# Revit family: 0068079
name_source: partatom
category: Lighting Fixtures
revit_build: Autodesk Revit 2017 (Build: 20190507_1515(x64)
units: mm (PartAtom-declared; Revit-internal decimal feet)

## family parameters
Cut with Voids When Loaded = No
Host = Face
Light Source = Yes
OmniClass Number = 23.80.70.11.14
OmniClass Title = General Luminaries, Directional
Part Type = Normal
Room Calculation Point = No
Round Connector Dimension = Use Diameter
Shared = No

## types (2) — shared parameters
AccessoryMaterial = Diffuser-Sylvania-Glow
Apparent Load = 24 VA
Assembly Code = D5020200
AssetType = Fixed
BodyMaterial = Body-Sylvania-Gray
ClassificationName = Uniclass2015
ClassificationValue = EF_70_80
Color Filter = 16777215
Default Elevation = 1219 mm
Description = Start Waterproof, integrated LED weatherproof luminaire, with UV stabilized flat diffuser and linear prisms designed to achieve uniform lit appearance, optimise light output and to reduce glare, stainless steel diffuser clips and fixing brackets for surface mounting. Glass Reinforced Plastic housing for robustness, Polycarbonate diffuser, 2750 lm, 24 W, 115 lm/W, 4000 K, drive current 350 mA, Non dimmable, 3 hours emergency,  CRI80, IP65, IK08, Class I,  nominal average life (h):50000, 1278 mm x 84 mm x 75 mm ,energy class: A++ A+ A, D-mark
DiffuserMaterial = Diffuser-Sylvania-Transparent
Dimming Lamp Color Temperature Shift = <None>
DocumentationLiterature = http://www.sylvania-lighting.com
DurationUnit = hours
ElectricShockClassification = Class I
Emit Shape Visible in Rendering = No
Emit from Rectangle Length = 1252 mm  [stored 4.10761 ft]
Emit from Rectangle Width = 64 mm  [stored 0.209974 ft]
ExpectedLife = 50000
IfcExportAs = IfcLightFixtureType
IfcExportType = IfcLightFixtureType
ImpactProtectionIndex = IK08
IngressProtection = IP65
Keynote = 16500
Lamp = LED
LampColourRenderingIndex = 80
LampColourTemperature = 4000 K
LampsType = LED
Length = 1272 mm  [stored 4.17323 ft]
Manufacturer = Feilo Sylvania
ManufacturerName = Feilo Sylvania
Material = composite material housing, pc polycarbonate diffuser
ModelNumber = 0068079
NominalHeight = 75 mm
NominalLength = 1278 mm  [stored 4.19291 ft]
PowerConsumption = 24 W
PowerFactor = 0.95
ReflectorMaterial = <By Category>
Tilt Angle = -90.00°
Type Image = <None>
URL = http://www.sylvania-lighting.com
Voltage = 0 V
Weight = 1.95 kg
Width = 84 mm  [stored 0.275591 ft]
zero-valued in all types: Cost, NominalWidth

## per-type parameters (varying)
| type | LampNominalLuminous | LuminousEfficacy | Model | ModelReference | Name | Photometric Web File | TypeName |
| 0068079 ST WTRPRF GRP S 1200 IP65 EM 2800LM 840 - Emergency mode | 234 lm | 9.761 lm/W | START Waterproof GRP Single 1200 IP65 EM 2800 840 - Emergency mode | START Waterproof GRP Single 1200 IP65 EM 2800 840 - Emergency mode | START Waterproof GRP Single 1200 IP65 EM 2800 840 - Emergency mode | 0068079EM.ies | START Waterproof GRP Single 1200 IP65 EM 2800 840 - Emergency mode |
| 0068079 ST WTRPRF GRP S 1200 IP65 EM 2800LM 840 | 2750 lm | 115 lm/W | START Waterproof GRP Single 1200 IP65 EM 2800 840 | START Waterproof GRP Single 1200 IP65 EM 2800 840 | START Waterproof GRP Single 1200 IP65 EM 2800 840 | 0068079.ies | START Waterproof GRP Single 1200 IP65 EM 2800 840 |

note: [stored X ft] marks values corroborated as IEEE doubles in the binary element streams (Revit-internal decimal feet)

## geometry (parser evidence)
native form markers: Sweep x3
no freeform markers — native parametric forms only
